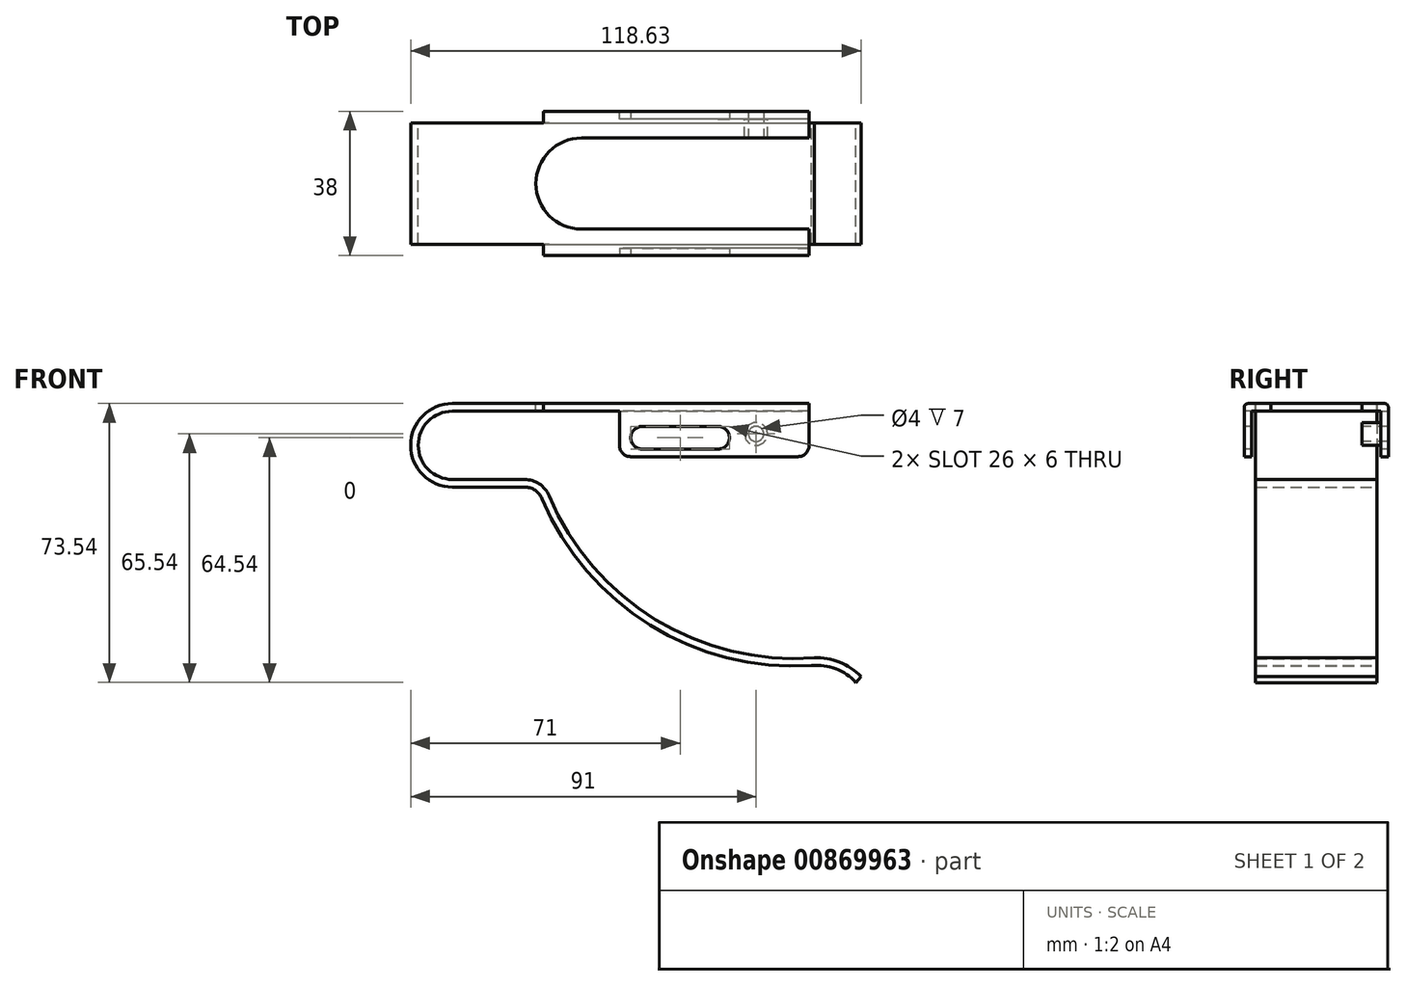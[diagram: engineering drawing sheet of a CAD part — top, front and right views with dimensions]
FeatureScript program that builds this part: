
annotation { "Feature Type Name" : "Feature", "Feature Type Description" : "" }
export const myFeature = defineFeature(function(context is Context, id is Id, definition is map)
    precondition{}
    {
        {
            var Q0;
            Q0=qCreatedBy(makeId("Front.planeOp"),FACE);
            var sketch = newSketch(context, id + "F0", { "sketchPlane" : qUnion([Q0])});
            skArc(sketch, "E0", {"start": v(0, 11) * mm, "mid": v(-11, 0) * mm, "end": v(0, -11) * mm});
            skLineSegment(sketch, "E1", {"start": v(0, 11) * mm, "end": v(94, 11) * mm});
            skLineSegment(sketch, "E2", {"start": v(0, -11) * mm, "end": v(19, -11) * mm});
            skArc(sketch, "E3", {"start": v(23.61, -14.06) * mm, "mid": v(52.09, -47.41) * mm, "end": v(94.63, -58.05) * mm});
            skArc(sketch, "E4", {"start": v(106.34, -62.54) * mm, "mid": v(101.02, -58.91) * mm, "end": v(94.63, -58.05) * mm});
            skPoint(sketch, "E5.visualSharp", {"position": v(22.4, -11) * mm});
            skArc(sketch, "E5.filletArc", {"start": v(23.61, -14.06) * mm, "mid": v(21.77, -11.84) * mm, "end": v(19, -11) * mm});
            skLineSegment(sketch, "E6.0", {"start": v(0, 9) * mm, "end": v(94, 9) * mm});
            skArc(sketch, "E6.1", {"start": v(0, 9) * mm, "mid": v(-9, 0) * mm, "end": v(0, -9) * mm});
            skArc(sketch, "E6.2", {"start": v(107.63, -61) * mm, "mid": v(102, -57.16) * mm, "end": v(95.3, -56) * mm});
            skArc(sketch, "E6.3", {"start": v(25.45, -13.3) * mm, "mid": v(53.48, -45.92) * mm, "end": v(95.3, -56) * mm});
            skArc(sketch, "E6.4", {"start": v(25.45, -13.3) * mm, "mid": v(22.88, -10.17) * mm, "end": v(19, -9) * mm});
            skLineSegment(sketch, "E6.5", {"start": v(0, -9) * mm, "end": v(19, -9) * mm});
            skLineSegment(sketch, "E7", {"start": v(94, 11) * mm, "end": v(94, 9) * mm});
            skLineSegment(sketch, "E8", {"start": v(107.63, -61) * mm, "end": v(106.34, -62.54) * mm});
            skSolve(sketch);
        }
        {
            var Q0;
            Q0=makeQuery(id+"F0.imprint","IMPRINT",FACE,{"disambiguationData":[TD([[makeQuery(id+"F0.imprint","IMPRINT",EDGE,{"derivedFrom":sQuery(id+"F0.wireOp",EDGE,"E0")}),1.0]])]});
            extrude(context, id + "F1", {"entities" : qUnion([Q0]), "depth" : 16 * mm, "offsetDistance" : 25 * mm});
        }
        {
            var Q0;
            Q0=makeQuery(id+"F1.opExtrude","SWEPT_FACE",FACE,{"disambiguationData":[OSD([sQuery(id+"F0.wireOp",EDGE,"E1")])]});
            var sketch = newSketch(context, id + "F2", { "sketchPlane" : qUnion([Q0])});
            skLineSegment(sketch, "E9.bottom", {"start": v(94, -16) * mm, "end": v(24, -16) * mm});
            skLineSegment(sketch, "E9.top", {"start": v(94, -19) * mm, "end": v(24, -19) * mm});
            skLineSegment(sketch, "E9.left", {"start": v(94, -16) * mm, "end": v(94, -19) * mm});
            skLineSegment(sketch, "E9.right", {"start": v(24, -16) * mm, "end": v(24, -19) * mm});
            skSolve(sketch);
        }
        {
            var Q0;
            Q0=makeQuery(id+"F2.imprint","IMPRINT",FACE,{"disambiguationData":[TD([[makeQuery(id+"F2.imprint","IMPRINT",EDGE,{"derivedFrom":sQuery(id+"F2.wireOp",EDGE,"E9.bottom")}),-1.0]])]});
            extrude(context, id + "F3", {"entities" : qUnion([Q0]), "operationType" : NewBodyOperationType.ADD, "oppositeDirection" : true, "depth" : 2 * mm, "offsetDistance" : 25 * mm});
        }
        {
            var Q0;
            Q0=makeQuery(id+"F3.opExtrude","SWEPT_FACE",FACE,{"disambiguationData":[OSD([sQuery(id+"F2.wireOp",EDGE,"E9.top")])]});
            var sketch = newSketch(context, id + "F4", { "sketchPlane" : qUnion([Q0])});
            skLineSegment(sketch, "E10.bottom", {"start": v(94, 11) * mm, "end": v(44, 11) * mm});
            skLineSegment(sketch, "E10.top", {"start": v(94, -3) * mm, "end": v(44, -3) * mm});
            skLineSegment(sketch, "E10.left", {"start": v(94, 11) * mm, "end": v(94, -3) * mm});
            skLineSegment(sketch, "E10.right", {"start": v(44, 11) * mm, "end": v(44, -3) * mm});
            skSolve(sketch);
        }
        {
            var Q0;
            {var subQ0=sQuery(id+"F4.wireOp",EDGE,"E10.top");Q0=makeQuery(id+"F4.imprint","IMPRINT",FACE,{"disambiguationData":[TD([[makeQuery(id+"F4.imprint","IMPRINT",EDGE,{"derivedFrom":subQ0}),-1.0]])]});}
            extrude(context, id + "F5", {"entities" : qUnion([Q0]), "operationType" : NewBodyOperationType.ADD, "oppositeDirection" : true, "depth" : 2 * mm, "offsetDistance" : 25 * mm});
        }
        {
            var Q0;
            Q0=makeQuery(id+"F3.opExtrude","CAP_EDGE",EDGE,{"disambiguationData":[OSD([sQuery(id+"F2.wireOp",EDGE,"E9.top")])],"isStart":true});
            var Q1;
            Q1=makeQuery(id+"F5.opExtrude","CAP_EDGE",EDGE,{"disambiguationData":[OSD([sQuery(id+"F2.wireOp",EDGE,"E9.top")])],"isStart":false});
            fillet(context, id + "F6", {"entities" : qUnion([Q0, Q1]), "radius" : 1 * mm, "allowEdgeOverflow" : false});
        }
        {
            var Q0;
            Q0=makeQuery(id+"F1.opExtrude","SWEPT_BODY",BODY,{"disambiguationData":[OSD([sQuery(id+"F0.wireOp",EDGE,"E0"),sQuery(id+"F0.wireOp",EDGE,"E1"),sQuery(id+"F0.wireOp",EDGE,"E2"),sQuery(id+"F0.wireOp",EDGE,"E3"),sQuery(id+"F0.wireOp",EDGE,"E4"),sQuery(id+"F0.wireOp",EDGE,"E5.filletArc"),sQuery(id+"F0.wireOp",EDGE,"E6.0"),sQuery(id+"F0.wireOp",EDGE,"E6.1"),sQuery(id+"F0.wireOp",EDGE,"E6.2"),sQuery(id+"F0.wireOp",EDGE,"E6.3"),sQuery(id+"F0.wireOp",EDGE,"E6.4"),sQuery(id+"F0.wireOp",EDGE,"E6.5"),sQuery(id+"F0.wireOp",EDGE,"E7"),sQuery(id+"F0.wireOp",EDGE,"E8")])]});
            var Q1;
            Q1=qCreatedBy(makeId("Front.planeOp"),FACE);
            mirror(context, id + "F7", {"operationType" : NewBodyOperationType.ADD, "entities" : qUnion([Q0]), "mirrorPlane" : qUnion([Q1])});
        }
        {
            var Q0;
            {var subQ0=makeQuery(id+"F3.boolean.opBoolean","MERGE",FACE,{"derivedFrom":[makeQuery(id+"F1.opExtrude","SWEPT_FACE",FACE,{"disambiguationData":[OSD([sQuery(id+"F0.wireOp",EDGE,"E1")])]}),makeQuery(id+"F3.opExtrude","CAP_FACE",FACE,{"disambiguationData":[OSD([sQuery(id+"F2.wireOp",EDGE,"E9.bottom"),sQuery(id+"F2.wireOp",EDGE,"E9.top"),sQuery(id+"F2.wireOp",EDGE,"E9.left"),sQuery(id+"F2.wireOp",EDGE,"E9.right")])],"isStart":true})]});Q0=makeQuery(id+"F7.boolean.opBoolean","MERGE",FACE,{"derivedFrom":[subQ0,makeQuery(id+"F7.opPattern","COPY",FACE,{"derivedFrom":subQ0,"instanceName":"1"})]});}
            var sketch = newSketch(context, id + "F8", { "sketchPlane" : qUnion([Q0])});
            skArc(sketch, "E11", {"start": v(34, 12) * mm, "mid": v(22, 0) * mm, "end": v(34, -12) * mm});
            skLineSegment(sketch, "E12", {"start": v(34, -12) * mm, "end": v(94, -12) * mm});
            skLineSegment(sketch, "E13", {"start": v(94, -12) * mm, "end": v(94, 12) * mm});
            skLineSegment(sketch, "E14", {"start": v(94, 12) * mm, "end": v(34, 12) * mm});
            skSolve(sketch);
        }
        {
            var Q0;
            Q0=makeQuery(id+"F8.imprint","IMPRINT",FACE,{"disambiguationData":[TD([[makeQuery(id+"F8.imprint","IMPRINT",EDGE,{"derivedFrom":sQuery(id+"F8.wireOp",EDGE,"E11")}),1.0]])]});
            extrude(context, id + "F9", {"entities" : qUnion([Q0]), "operationType" : NewBodyOperationType.REMOVE, "oppositeDirection" : true, "depth" : 2 * mm, "offsetDistance" : 25 * mm});
        }
        {
            var Q0;
            {var subQ0=sQuery(id+"F2.wireOp",EDGE,"E9.top");Q0=makeQuery(id+"F5.boolean.opBoolean","MERGE",FACE,{"derivedFrom":[makeQuery(id+"F3.opExtrude","SWEPT_FACE",FACE,{"disambiguationData":[OSD([subQ0])]}),makeQuery(id+"F5.opExtrude","CAP_FACE",FACE,{"disambiguationData":[OSD([subQ0,sQuery(id+"F4.wireOp",EDGE,"E10.top"),sQuery(id+"F4.wireOp",EDGE,"E10.left"),sQuery(id+"F4.wireOp",EDGE,"E10.right")])],"isStart":true})]});}
            var sketch = newSketch(context, id + "F10", { "sketchPlane" : qUnion([Q0])});
            skLineSegment(sketch, "E15", {"start": v(50, 2) * mm, "end": v(70, 2) * mm});
            skArc(sketch, "E16.0.startCap", {"start": v(50, -1) * mm, "mid": v(47, 2) * mm, "end": v(50, 5) * mm});
            skArc(sketch, "E16.0.endCap", {"start": v(70, 5) * mm, "mid": v(73, 2) * mm, "end": v(70, -1) * mm});
            skLineSegment(sketch, "E16.0.left", {"start": v(50, 5) * mm, "end": v(70, 5) * mm});
            skLineSegment(sketch, "E16.0.right", {"start": v(50, -1) * mm, "end": v(70, -1) * mm});
            skSolve(sketch);
        }
        {
            var Q0;
            Q0 = qSketchRegion(id + "F10", true);
            extrude(context, id + "F11", {"entities" : qUnion([Q0]), "operationType" : NewBodyOperationType.REMOVE, "endBound" : BoundingType.THROUGH_ALL, "oppositeDirection" : true, "depth" : 25 * mm, "offsetDistance" : 25 * mm});
        }
        {
            var Q0;
            Q0=qCreatedBy(makeId("Front.planeOp"),FACE);
            var sketch = newSketch(context, id + "F12", { "sketchPlane" : qUnion([Q0])});
            skPoint(sketch, "E17", {"position": v(80, 3) * mm});
            skSolve(sketch);
        }
        {
            var Q0;
            Q0=sQuery(id+"F12.wireOp",VERTEX,"E17");
            var Q1;
            Q1=makeQuery(id+"F1.opExtrude","SWEPT_BODY",BODY,{"disambiguationData":[OSD([sQuery(id+"F0.wireOp",EDGE,"E0"),sQuery(id+"F0.wireOp",EDGE,"E1"),sQuery(id+"F0.wireOp",EDGE,"E2"),sQuery(id+"F0.wireOp",EDGE,"E3"),sQuery(id+"F0.wireOp",EDGE,"E4"),sQuery(id+"F0.wireOp",EDGE,"E5.filletArc"),sQuery(id+"F0.wireOp",EDGE,"E6.0"),sQuery(id+"F0.wireOp",EDGE,"E6.1"),sQuery(id+"F0.wireOp",EDGE,"E6.2"),sQuery(id+"F0.wireOp",EDGE,"E6.3"),sQuery(id+"F0.wireOp",EDGE,"E6.4"),sQuery(id+"F0.wireOp",EDGE,"E6.5"),sQuery(id+"F0.wireOp",EDGE,"E7"),sQuery(id+"F0.wireOp",EDGE,"E8")])]});
            hole(context, id + "F13", {"style" : HoleStyle.SIMPLE, "endStyle" : HoleEndStyle.THROUGH, "holeDiameter" : 4 * mm, "majorDiameter" : 5 * mm, "isTappedThrough" : true, "tappedDepth" : 12 * mm, "tapClearance" : 3, "locations" : qUnion([Q0]), "scope" : qUnion([Q1])});
        }
        {
            var Q0;
            Q0=makeQuery(id+"F7.opPattern","COPY",FACE,{"derivedFrom":makeQuery(id+"F5.opExtrude","CAP_FACE",FACE,{"disambiguationData":[OSD([sQuery(id+"F2.wireOp",EDGE,"E9.top"),sQuery(id+"F4.wireOp",EDGE,"E10.top"),sQuery(id+"F4.wireOp",EDGE,"E10.left"),sQuery(id+"F4.wireOp",EDGE,"E10.right")])],"isStart":false}),"instanceName":"1"});
            var sketch = newSketch(context, id + "F14", { "sketchPlane" : qUnion([Q0])});
            skCircle(sketch, "E18.0", {"center": v(80, 3) * mm, "radius": 2 * mm});
            skCircle(sketch, "E19.0", {"center": v(80, 3) * mm, "radius": 3 * mm});
            skSolve(sketch);
        }
        {
            var Q0;
            Q0=makeQuery(id+"F14.imprint","IMPRINT",FACE,{"disambiguationData":[TD([[makeQuery(id+"F14.imprint","IMPRINT",EDGE,{"derivedFrom":sQuery(id+"F14.wireOp",EDGE,"E18.0")}),-1.0]])]});
            extrude(context, id + "F15", {"entities" : qUnion([Q0]), "operationType" : NewBodyOperationType.ADD, "depth" : 5 * mm, "offsetDistance" : 25 * mm});
        }
        {
            var Q0;
            Q0=makeQuery(id+"F5.opExtrude","SWEPT_EDGE",EDGE,{"disambiguationData":[OSD([sQuery(id+"F4.wireOp",EDGE,"E10.top"),sQuery(id+"F4.wireOp",EDGE,"E10.left")])]});
            var Q1;
            Q1=makeQuery(id+"F7.opPattern","COPY",EDGE,{"derivedFrom":makeQuery(id+"F5.opExtrude","SWEPT_EDGE",EDGE,{"disambiguationData":[OSD([sQuery(id+"F4.wireOp",EDGE,"E10.top"),sQuery(id+"F4.wireOp",EDGE,"E10.left")])]}),"instanceName":"1"});
            var Q2;
            Q2=makeQuery(id+"F5.opExtrude","SWEPT_EDGE",EDGE,{"disambiguationData":[OSD([sQuery(id+"F4.wireOp",EDGE,"E10.top"),sQuery(id+"F4.wireOp",EDGE,"E10.right")])]});
            var Q3;
            Q3=makeQuery(id+"F7.opPattern","COPY",EDGE,{"derivedFrom":makeQuery(id+"F5.opExtrude","SWEPT_EDGE",EDGE,{"disambiguationData":[OSD([sQuery(id+"F4.wireOp",EDGE,"E10.top"),sQuery(id+"F4.wireOp",EDGE,"E10.right")])]}),"instanceName":"1"});
            fillet(context, id + "F16", {"entities" : qUnion([Q0, Q1, Q2, Q3]), "radius" : 3 * mm, "tangentPropagation" : true, "allowEdgeOverflow" : false});
        }
    });
